# Revit family: PRD_AR_TltPprDspnsrs_STRATOSToiletSeatPaperDispenser_STR680
name_source: partatom
category: Specialty Equipment
units: mm (PartAtom-declared; Revit-internal decimal feet)

## family parameters
Cut with Voids When Loaded = No
Host = Face
OmniClass Number = 23.40.20.21.21
OmniClass Title = Toilet Paper Dispensers
Part Type = Normal
Room Calculation Point = No
Round Connector Dimension = Use Diameter
Shared = No

## types (1)
- STR680
    AssetType = Fixed
    BIMObjectName = PRD_AR_ToiletPaperDispensers_STRATOSToiletSeatPaperDispenser_STR680
    Category = Pr_40_70_22_90, Toilet paper dispensers
    Default Elevation = 700 mm  [stored 2.29659 ft]
    Description = STRATOS toilet seat paper dispenser for wall mounting, stainless steel, surface satin finished, material thickness 1.5 mm, curved front with oval opening, cylinder lock with key, for seat paper E-STRX680, incl. mounting material.
    DispenserMaterial = PRD_AR_StainlessSteel_SatinFinished
    DurationUnit = year
    Features = stainless steel, surface satin finished
    FillingQuantity = 200
    FillingQuantityUom = Pieces
    Finish = satin finished
    GrossWeight = 3.36 kg
    IfcExportAs = IfcFurnitureType
    IfcExportType = USERDEFINED
    IntegralAccessories = incl. stainless steel screws and dowels
    IsBuiltIn = TRUE
    Lock = Key-lock
    MainColor = stainless steel
    Manufacturer = KWC Group Management AG
    ManufacturerName = KWC Group Management AG
    ManufacturerURL = www.kwc-professional.com
    Material = stainless steel
    MaterialCode = 1.4301
    MaterialThickness = 1.50 mm
    Model = STR680
    ModelNumber = 3600008877
    ModelReference = STR680
    NBSDescription = Toilet paper bulk dispensers
    NBSReference = 45-35-72/366
    Name = STRATOS Toilet seat paper dispenser STR680
    NetWeight = 2.72 kg
    NominalDepth = 54 mm  [stored 0.177165 ft]
    NominalHeight = 263 mm  [stored 0.862861 ft]
    NominalWidth = 393 mm  [stored 1.28937 ft]
    ProductInformation = http://pim.kwc.com
    Size = 393 x 263 x 54 mm
    Style = dispenser
    TypeOfConsumable = Toilet seat paper
    TypeOfFixing = Screw
    TypeOfMounting = Wall mounting
    TypeOfOperation = Manual operation
    URL = www.kwc-professional.com
    Uniclass2015Code = Pr_40_70_22_90
    Uniclass2015Title = Toilet paper dispensers
    Uniclass2015Version = Products v1.10
    Version = 1
    WarrantyDurationUnit = year

note: [stored X ft] marks values corroborated as IEEE doubles in the binary element streams (Revit-internal decimal feet)

## geometry (parser evidence)
native form markers: Sweep x2
no freeform markers — native parametric forms only
